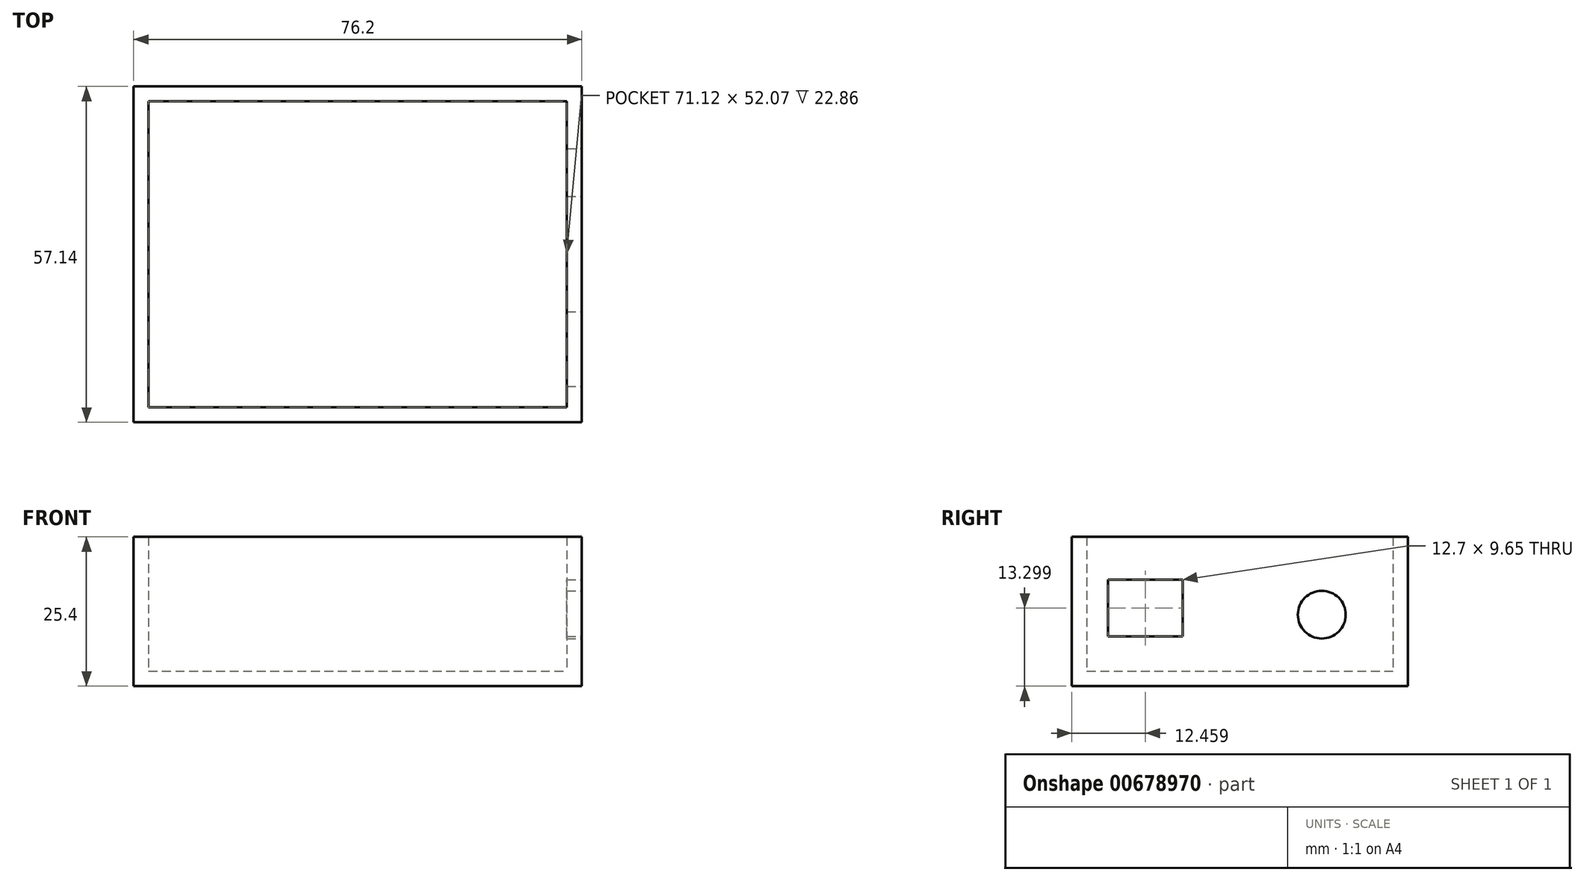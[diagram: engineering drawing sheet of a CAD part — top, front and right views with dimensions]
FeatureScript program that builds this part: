
annotation { "Feature Type Name" : "Feature", "Feature Type Description" : "" }
export const myFeature = defineFeature(function(context is Context, id is Id, definition is map)
    precondition{}
    {
        {
            var Q0;
            Q0=qCreatedBy(makeId("Front.planeOp"),FACE);
            var sketch = newSketch(context, id + "F0", { "sketchPlane" : qUnion([Q0])});
            skLineSegment(sketch, "E0.bottom", {"start": v(-38, -0.8) * mm, "end": v(38.2, -0.8) * mm});
            skLineSegment(sketch, "E0.top", {"start": v(-38, -26.2) * mm, "end": v(38.2, -26.2) * mm});
            skLineSegment(sketch, "E0.left", {"start": v(-38, -0.8) * mm, "end": v(-38, -26.2) * mm});
            skLineSegment(sketch, "E0.right", {"start": v(38.2, -0.8) * mm, "end": v(38.2, -26.2) * mm});
            skSolve(sketch);
        }
        {
            var Q0;
            Q0 = qSketchRegion(id + "F0", true);
            extrude(context, id + "F1", {"entities" : qUnion([Q0]), "endBound" : BoundingType.SYMMETRIC, "depth" : 57.15 * mm, "offsetDistance" : 25.4 * mm});
        }
        {
            var Q0;
            Q0=makeQuery(id+"F1.opExtrude","SWEPT_FACE",FACE,{"disambiguationData":[OSD([sQuery(id+"F0.wireOp",EDGE,"E0.bottom")])]});
            shell(context, id + "F2", {"entities" : qUnion([Q0]), "thickness" : 2.54 * mm});
        }
        {
            var Q0;
            Q0=makeQuery(id+"F1.opExtrude","SWEPT_FACE",FACE,{"disambiguationData":[OSD([sQuery(id+"F0.wireOp",EDGE,"E0.right")])]});
            var sketch = newSketch(context, id + "F3", { "sketchPlane" : qUnion([Q0])});
            skCircle(sketch, "E1", {"center": v(13.91, -14.02) * mm, "radius": 4.06 * mm});
            skSolve(sketch);
        }
        {
            var Q0;
            Q0=makeQuery(id+"F3.imprint","IMPRINT",FACE,{"disambiguationData":[TD([[makeQuery(id+"F3.imprint","IMPRINT",EDGE,{"derivedFrom":sQuery(id+"F3.wireOp",EDGE,"E1")}),1.0]])]});
            extrude(context, id + "F4", {"entities" : qUnion([Q0]), "operationType" : NewBodyOperationType.REMOVE, "endBound" : BoundingType.UP_TO_NEXT, "oppositeDirection" : true, "depth" : 25.4 * mm, "offsetDistance" : 25.4 * mm});
        }
        {
            var Q0;
            Q0=makeQuery(id+"F1.opExtrude","SWEPT_FACE",FACE,{"disambiguationData":[OSD([sQuery(id+"F0.wireOp",EDGE,"E0.right")])]});
            var sketch = newSketch(context, id + "F5", { "sketchPlane" : qUnion([Q0])});
            skLineSegment(sketch, "E2.bottom", {"start": v(-22.46, -8.06) * mm, "end": v(-9.76, -8.06) * mm});
            skLineSegment(sketch, "E2.top", {"start": v(-22.46, -17.72) * mm, "end": v(-9.76, -17.72) * mm});
            skLineSegment(sketch, "E2.left", {"start": v(-22.46, -8.06) * mm, "end": v(-22.46, -17.72) * mm});
            skLineSegment(sketch, "E2.right", {"start": v(-9.76, -8.06) * mm, "end": v(-9.76, -17.72) * mm});
            skSolve(sketch);
        }
        {
            var Q0;
            Q0 = qSketchRegion(id + "F5", true);
            extrude(context, id + "F6", {"entities" : qUnion([Q0]), "operationType" : NewBodyOperationType.REMOVE, "endBound" : BoundingType.UP_TO_NEXT, "oppositeDirection" : true, "depth" : 25.4 * mm, "offsetDistance" : 25.4 * mm});
        }
    });
